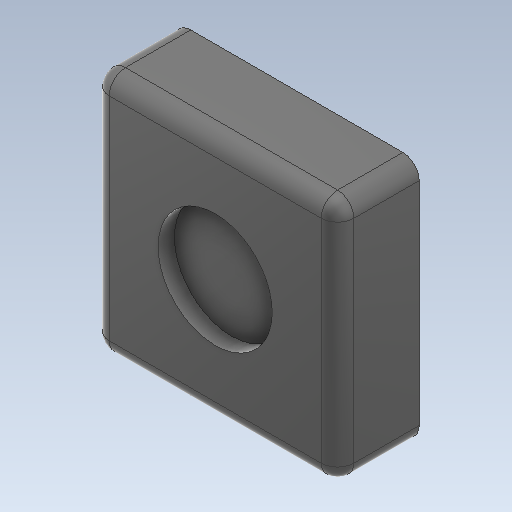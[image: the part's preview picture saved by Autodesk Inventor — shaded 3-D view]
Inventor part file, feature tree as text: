
AUTODESK INVENTOR PART (.ipt)
format: ipt  version: 2020 (Build 240168000, 168)  size: 140,288 bytes
history: native  units: mm
features: extrude x2, sketch x2, fillet x1
ambient origin geometry x8: Origin, YZ Plane, XZ Plane, XY Plane, X Axis, Y Axis, Z Axis, Center Point
bodies: Solid1 (feature_tree)
feature tree (5):
  extrude  "Extrusion1"  Depth=30.0mm
  extrude  "Extrusion2"  Depth=2.0mm
  fillet  "Fillet1"  Radius=2.0mm
  sketch  "Sketch1"  dims[d0=30.0mm d1=30.0mm]
  sketch  "Sketch2"  dims[d2=10.0mm d3=0.0mm d4=14.0mm d5=2.0mm d6=0.0mm d7=2.0mm]
